# Revit family: Sanitary_Toilets_Johnson-Suisse_Egg_Junior_Toilet_Suite
name_source: partatom
category: Plumbing Fixtures
revit_build: Autodesk Revit 2015 (Build: 20140606_1530(x64)
units: mm (PartAtom-declared; Revit-internal decimal feet)

## types (5) — shared parameters
BIMobject category = Toilets
Brand url = http://www.johnsonsuisse.com.au
Design country = Thailand
EAN code = https://8852425133298
Edition number = 1
IFC Classification = Sanitary Terminal
Manufacturer country = Thailand
Manufacturer name = Johnson Suisse
Material main = Vitreous china
NBS Reference Code = 35-65-90
NBS Reference Description = Toilet Systems
Nominal height = 730 mm  [stored 2.39501 ft]
Nominal width = 365 mm  [stored 1.19751 ft]
Product Guid = f991ba34-6298-452e-ada1-bf97fcbf3db8
Product SKU = C67977_C6262_X011H
Product data url = https://bimobject.com
Product family = Egg
Product group = Toilet Suites
Product url = https://johnsonsuisse.com.au
QR code = http://bimobject.com
Technical description = https://johnsonsuisse.com.au
UNSPSC Code = 301815
Uniclass 1.4 Code = L7216
Uniclass 1.4 Description = Toilets
Uniclass 2.0 Code = SS-35-65-90
Uniclass 2.0 Description = Toilet Systems
Uniclass 2015 Code = SL_35_80_89
Uniclass 2015 Name = Toilets
Weight Net (Kg) = 0

## per-type parameters (varying)
| type | Type |
| Egg Junior Toilet Suite Green | egg_junior_toilet_suite : Cistern Lid Color - (Green) |
| Egg Junior Toilet Suite Lemon | egg_junior_toilet_suite : Cistern Lid Color - (Lemon) |
| Egg Junior Toilet Suite Rose | egg_junior_toilet_suite : Cistern Lid Color - (Rose) |
| Egg Junior Toilet Suite Blue | egg_junior_toilet_suite : Cistern Lid Color - (Blue) |
| Egg Junior Toilet Suite White | egg_junior_toilet_suite : Cistern Lid Color - (White) |

note: [stored X ft] marks values corroborated as IEEE doubles in the binary element streams (Revit-internal decimal feet)

## geometry (parser evidence)
native form markers: Sweep x6
no freeform markers — native parametric forms only
